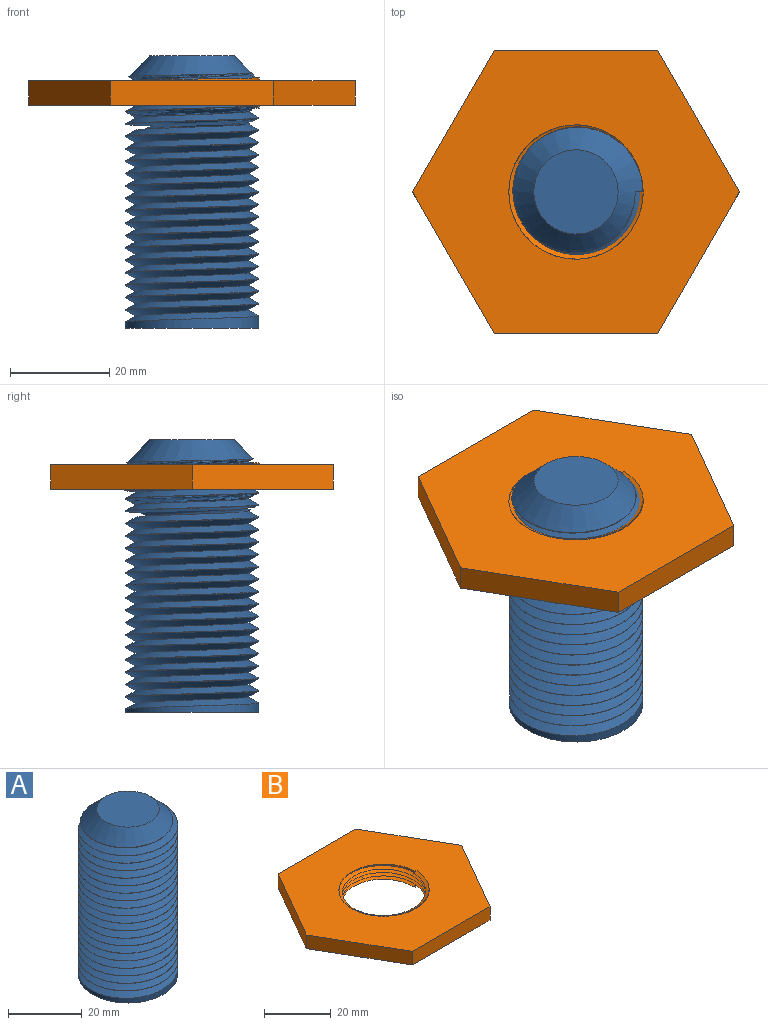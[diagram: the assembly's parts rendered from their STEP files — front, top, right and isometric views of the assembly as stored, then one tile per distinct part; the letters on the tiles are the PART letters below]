
ASSEMBLY  parts=2 mates=1
PART A: 8 faces, bbox 27x31.2x55 mm
  f0: cylinder r=13.5mm len=50mm, axis (0,0,-1), area -1860.7mm2, adj f1,f3,f5,f6,f7
  f1: cone r=8.5mm half-angle=45deg, axis (0,0,-1), area 401mm2, adj f0,f2,f4,f6
  f2: plane 17x17mm, normal (0,0,1), area 227mm2, adj f1
  f3: plane 27x27mm, normal (0,0,-1), area 572.6mm2, adj f0
  f4: plane 2.19x1.56mm, normal (0,-1,0), area 0.8mm2, adj f1,f6,f7
  f5: plane 2.43x2.19mm, normal (0,1,0), area 2.7mm2, adj f0,f6,f7
  f6: bspline ~51.22x26.99mm, area 3805.1mm2, adj f0,f1,f4,f5,f7
  f7: bspline ~51.22x31.18mm, area 3768.7mm2, adj f0,f4,f5,f6
PART B: 15 faces, bbox 66x57.1x6.2 mm
  f0: cylinder r=13.55mm len=27.1mm, axis (0,0,-1), area 40.7mm2, adj f7,f8,f10,f11,f13,f14
  f1: plane 32.97x5mm, normal (0,1,0), area 164.8mm2, adj f2,f6,f7,f8
  f2: plane 28.55x16.48mm, normal (-0.87,0.5,0), area 164.8mm2, adj f1,f3,f7,f8
  f3: plane 28.55x16.48mm, normal (-0.87,-0.5,0), area 164.8mm2, adj f2,f4,f7,f8
  f4: plane 32.97x5mm, normal (0,-1,0), area 164.8mm2, adj f3,f5,f7,f8
  f5: plane 28.55x16.48mm, normal (0.87,-0.5,0), area 164.8mm2, adj f4,f6,f7,f8
  f6: plane 28.55x16.48mm, normal (0.87,0.5,0), area 164.8mm2, adj f1,f5,f7,f8
  f7: plane 65.96x57.12mm, normal (0,0,1), area 2246.6mm2, adj f0,f1,f2,f3,f4,f5,f6,f12
  f8: plane 65.96x57.12mm, normal (0,0,-1), area 2246.8mm2, adj f0,f1,f2,f3,f4,f5,f6,f9
  f9: cylinder r=13.55mm len=26.98mm, axis (0,0,-1), area 12.2mm2, adj f8,f11,f14
  f10: plane 1.2x1.04mm, normal (0,1,0), area 0.6mm2, adj f0,f12,f13,f14
  f11: plane 1.2x1.04mm, normal (0,-1,0), area 0.6mm2, adj f0,f9,f13,f14
  f12: cylinder r=13.55mm len=26.98mm, axis (0,0,-1), area 12.2mm2, adj f7,f10,f13
  f13: bspline ~27.09x27.08mm, area 393.3mm2, adj f0,f7,f10,f11,f12,f14
  f14: bspline ~27.09x27.08mm, area 393.4mm2, adj f0,f8,f9,f10,f11,f13
PLACE A t=(25.76,18.78,-18.39)mm
PLACE B t=(25.76,18.78,26.61)mm
MATE fastened B.f0 <-> A.f0  axis (0,0,-1) through (25.76,18.78,26.61)mm
